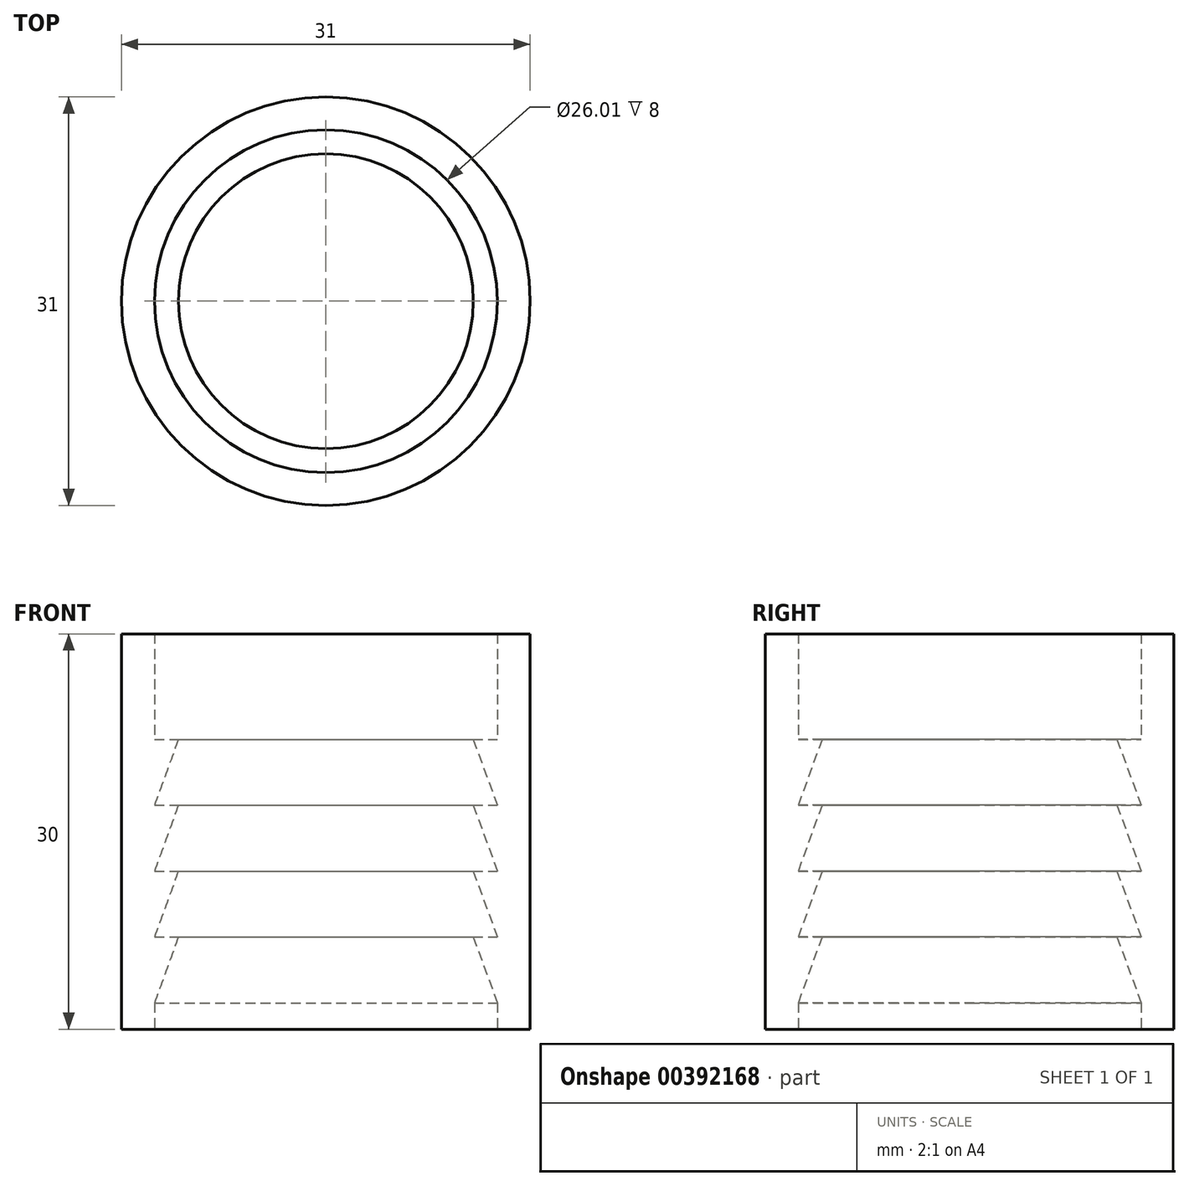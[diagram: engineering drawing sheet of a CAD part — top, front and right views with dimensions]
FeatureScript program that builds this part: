
annotation { "Feature Type Name" : "Feature", "Feature Type Description" : "" }
export const myFeature = defineFeature(function(context is Context, id is Id, definition is map)
    precondition{}
    {
        {
            var Q0;
            Q0=qCreatedBy(makeId("Front.planeOp"),FACE);
            var sketch = newSketch(context, id + "F0", { "sketchPlane" : qUnion([Q0])});
            skLineSegment(sketch, "E0", {"start": v(13, 0) * mm, "end": v(15.5, 0) * mm});
            skLineSegment(sketch, "E1", {"start": v(15.5, 0) * mm, "end": v(15.5, 30) * mm});
            skLineSegment(sketch, "E2", {"start": v(15.5, 30) * mm, "end": v(13, 30) * mm});
            skLineSegment(sketch, "E3", {"start": v(13, 0) * mm, "end": v(13, 2) * mm});
            skLineSegment(sketch, "E4", {"start": v(13, 2) * mm, "end": v(11.18, 7) * mm});
            skLineSegment(sketch, "E5", {"start": v(11.18, 7) * mm, "end": v(13, 7) * mm});
            skLineSegment(sketch, "E6", {"start": v(13, 7) * mm, "end": v(11.18, 12) * mm});
            skLineSegment(sketch, "E7", {"start": v(11.18, 12) * mm, "end": v(13, 12) * mm});
            skLineSegment(sketch, "E8", {"start": v(13, 12) * mm, "end": v(11.18, 17) * mm});
            skLineSegment(sketch, "E9", {"start": v(11.18, 17) * mm, "end": v(13, 17) * mm});
            skLineSegment(sketch, "E10", {"start": v(13, 17) * mm, "end": v(11.18, 22) * mm});
            skLineSegment(sketch, "E11", {"start": v(11.18, 22) * mm, "end": v(13, 22) * mm});
            skLineSegment(sketch, "E12", {"start": v(13, 22) * mm, "end": v(13, 30) * mm});
            skLineSegment(sketch, "E13", {"start": v(0, 0) * mm, "end": v(0, 7.93) * mm});
            skSolve(sketch);
        }
        {
            var Q0;
            Q0=makeQuery(id+"F0.imprint","IMPRINT",FACE,{"disambiguationData":[TD([[makeQuery(id+"F0.imprint","IMPRINT",EDGE,{"derivedFrom":sQuery(id+"F0.wireOp",EDGE,"E0")}),1.0]])]});
            var Q1;
            Q1=sQuery(id+"F0.wireOp",EDGE,"E13");
            revolve(context, id + "F1", {"entities" : qUnion([Q0]), "axis" : qUnion([Q1]), "revolveType" : RevolveType.FULL});
        }
    });
